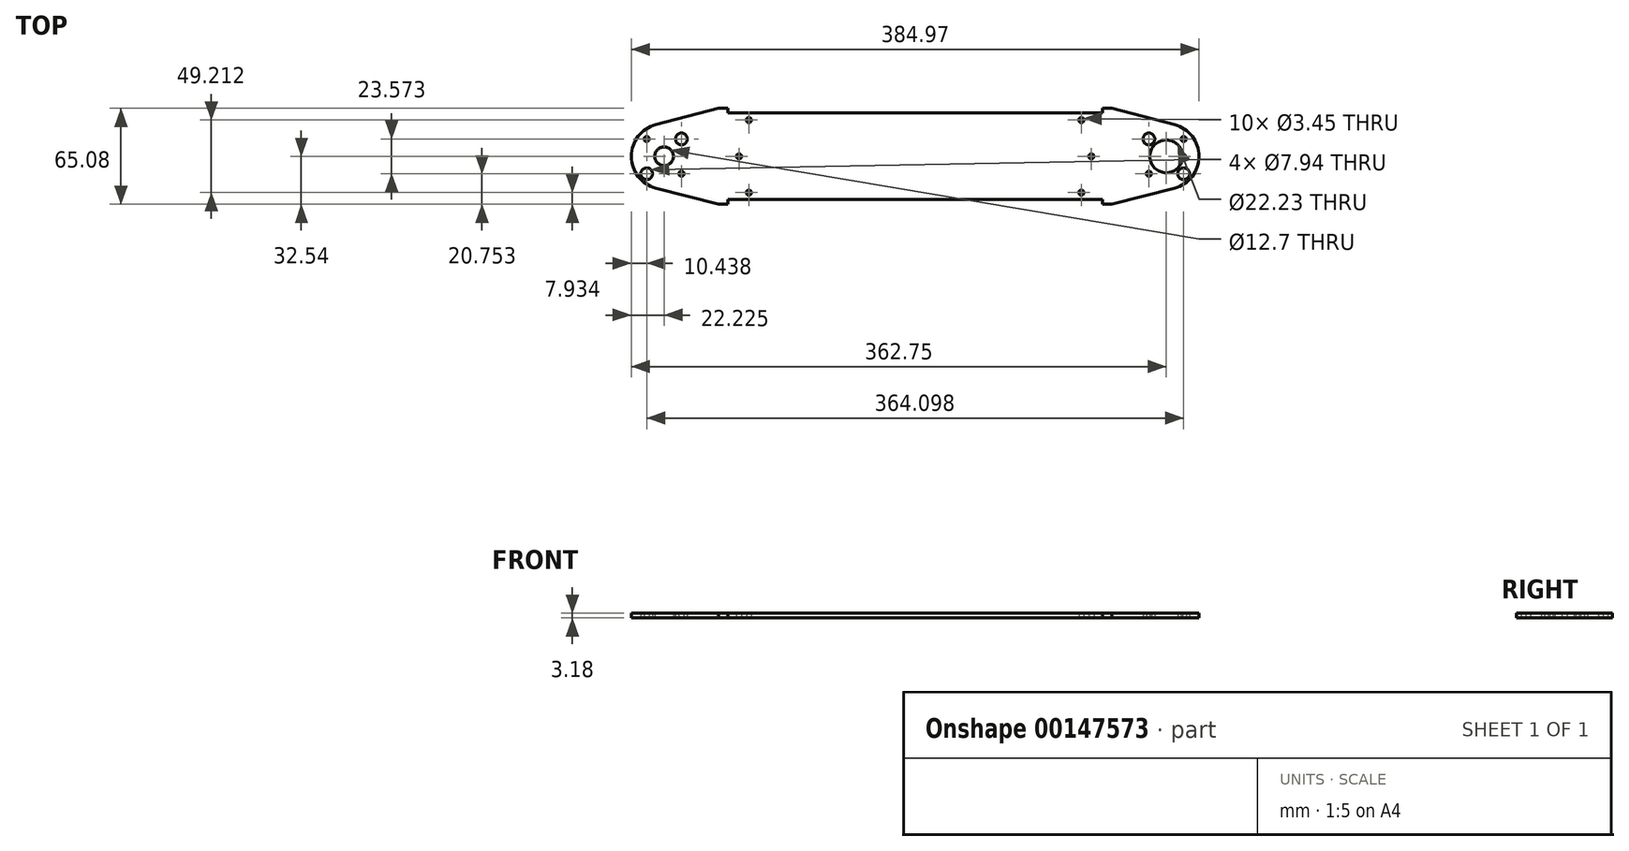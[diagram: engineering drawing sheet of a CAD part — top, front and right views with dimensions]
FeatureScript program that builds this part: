
annotation { "Feature Type Name" : "Feature", "Feature Type Description" : "" }
export const myFeature = defineFeature(function(context is Context, id is Id, definition is map)
    precondition{}
    {
        {
            var Q0;
            Q0=qCreatedBy(makeId("Top.planeOp"),FACE);
            var sketch = newSketch(context, id + "F0", { "sketchPlane" : qUnion([Q0])});
            skPoint(sketch, "E0.rect.middle", {"position": v(0, 0) * mm});
            skCircle(sketch, "E1", {"center": v(0, 0) * mm, "radius": 11.11 * mm});
            skLineSegment(sketch, "E2.bottom", {"start": v(11.79, 11.79) * mm, "end": v(-11.79, 11.79) * mm, "construction": true});
            skLineSegment(sketch, "E2.left", {"start": v(11.79, 11.79) * mm, "end": v(11.79, -11.79) * mm, "construction": true});
            skLineSegment(sketch, "E2.right", {"start": v(-11.79, 11.79) * mm, "end": v(-11.79, -11.79) * mm, "construction": true});
            skCircle(sketch, "E3", {"center": v(11.79, 11.79) * mm, "radius": 5.56 * mm, "construction": true});
            skCircle(sketch, "E4", {"center": v(-11.79, 11.79) * mm, "radius": 3.97 * mm});
            skCircle(sketch, "E5", {"center": v(11.79, 11.79) * mm, "radius": 1.73 * mm});
            skCircle(sketch, "E6", {"center": v(11.79, -11.79) * mm, "radius": 3.97 * mm});
            skCircle(sketch, "E7", {"center": v(-11.79, -11.79) * mm, "radius": 1.73 * mm});
            skArc(sketch, "E8", {"start": v(-346.1, 21.51) * mm, "mid": v(-362.75, 0) * mm, "end": v(-346.1, -21.51) * mm});
            skLineSegment(sketch, "E9.bottom", {"start": v(-352.31, 11.79) * mm, "end": v(-328.74, 11.79) * mm, "construction": true});
            skLineSegment(sketch, "E9.top", {"start": v(-352.31, -11.79) * mm, "end": v(-328.74, -11.79) * mm, "construction": true});
            skLineSegment(sketch, "E9.left", {"start": v(-352.31, 11.79) * mm, "end": v(-352.31, -11.79) * mm, "construction": true});
            skLineSegment(sketch, "E9.right", {"start": v(-328.74, 11.79) * mm, "end": v(-328.74, -11.79) * mm, "construction": true});
            skCircle(sketch, "E10", {"center": v(-328.74, 11.79) * mm, "radius": 3.97 * mm});
            skCircle(sketch, "E11", {"center": v(-352.31, 11.79) * mm, "radius": 1.73 * mm});
            skCircle(sketch, "E12", {"center": v(-352.31, -11.79) * mm, "radius": 3.97 * mm});
            skCircle(sketch, "E13", {"center": v(-328.74, -11.79) * mm, "radius": 1.73 * mm});
            skLineSegment(sketch, "E14", {"start": v(0, 0) * mm, "end": v(-340.53, 0) * mm, "construction": true});
            skLineSegment(sketch, "E15", {"start": v(-346.1, -21.51) * mm, "end": v(-303.61, -32.54) * mm});
            skLineSegment(sketch, "E16", {"start": v(-346.1, 21.51) * mm, "end": v(-303.61, 32.54) * mm});
            skLineSegment(sketch, "E17", {"start": v(-297.26, -29.37) * mm, "end": v(-43.26, -29.37) * mm});
            skLineSegment(sketch, "E18", {"start": v(-297.26, 29.37) * mm, "end": v(-43.26, 29.37) * mm});
            skLineSegment(sketch, "E19", {"start": v(-297.26, 32.54) * mm, "end": v(-297.26, 29.37) * mm});
            skLineSegment(sketch, "E20", {"start": v(-297.26, 32.54) * mm, "end": v(-303.61, 32.54) * mm});
            skLineSegment(sketch, "E21", {"start": v(-297.26, -29.37) * mm, "end": v(-297.26, -32.54) * mm});
            skLineSegment(sketch, "E22", {"start": v(-297.26, -32.54) * mm, "end": v(-303.61, -32.54) * mm});
            skLineSegment(sketch, "E23", {"start": v(-43.26, -29.37) * mm, "end": v(-43.26, -32.54) * mm});
            skLineSegment(sketch, "E24", {"start": v(-43.26, -32.54) * mm, "end": v(-36.91, -32.54) * mm});
            skLineSegment(sketch, "E25", {"start": v(-43.26, 29.37) * mm, "end": v(-43.26, 32.54) * mm});
            skLineSegment(sketch, "E26", {"start": v(-43.26, 32.54) * mm, "end": v(-36.91, 32.54) * mm});
            skLineSegment(sketch, "E27", {"start": v(-36.91, -32.54) * mm, "end": v(5.58, -21.51) * mm});
            skLineSegment(sketch, "E28", {"start": v(5.58, 21.51) * mm, "end": v(-36.91, 32.54) * mm});
            skArc(sketch, "E29", {"start": v(5.58, -21.51) * mm, "mid": v(22.23, 0) * mm, "end": v(5.58, 21.51) * mm});
            skLineSegment(sketch, "E30", {"start": v(-297.26, 29.37) * mm, "end": v(-297.26, 24.6) * mm, "construction": true});
            skLineSegment(sketch, "E31", {"start": v(-297.26, 24.6) * mm, "end": v(-282.98, 24.6) * mm, "construction": true});
            skLineSegment(sketch, "E32", {"start": v(-297.26, -29.37) * mm, "end": v(-297.26, -24.6) * mm, "construction": true});
            skLineSegment(sketch, "E33", {"start": v(-297.26, -24.6) * mm, "end": v(-282.98, -24.6) * mm, "construction": true});
            skLineSegment(sketch, "E34", {"start": v(-43.26, -29.37) * mm, "end": v(-43.26, -24.6) * mm, "construction": true});
            skLineSegment(sketch, "E35", {"start": v(-43.26, -24.6) * mm, "end": v(-57.55, -24.6) * mm, "construction": true});
            skLineSegment(sketch, "E36", {"start": v(-43.26, 29.37) * mm, "end": v(-43.26, 24.6) * mm, "construction": true});
            skLineSegment(sketch, "E37", {"start": v(-43.26, 24.6) * mm, "end": v(-57.55, 24.6) * mm, "construction": true});
            skCircle(sketch, "E38", {"center": v(-282.98, 24.6) * mm, "radius": 1.73 * mm});
            skCircle(sketch, "E39", {"center": v(-57.55, 24.6) * mm, "radius": 1.73 * mm});
            skCircle(sketch, "E40", {"center": v(-57.55, -24.6) * mm, "radius": 1.73 * mm});
            skCircle(sketch, "E41", {"center": v(-282.98, -24.6) * mm, "radius": 1.73 * mm});
            skLineSegment(sketch, "E42", {"start": v(-11.79, -11.79) * mm, "end": v(11.79, -11.79) * mm, "construction": true});
            skLineSegment(sketch, "E43", {"start": v(-170.26, -29.37) * mm, "end": v(-170.26, 0) * mm, "construction": true});
            skLineSegment(sketch, "E44", {"start": v(-170.26, 0) * mm, "end": v(-170.26, 29.37) * mm, "construction": true});
            skLineSegment(sketch, "E45", {"start": v(-328.74, 11.79) * mm, "end": v(-289.73, 11.79) * mm, "construction": true});
            skLineSegment(sketch, "E46", {"start": v(-289.73, 11.79) * mm, "end": v(-289.73, 0) * mm, "construction": true});
            skLineSegment(sketch, "E47", {"start": v(-11.79, 11.79) * mm, "end": v(-50.8, 11.79) * mm, "construction": true});
            skLineSegment(sketch, "E48", {"start": v(-50.8, 11.79) * mm, "end": v(-50.8, 0) * mm, "construction": true});
            skCircle(sketch, "E49", {"center": v(-50.8, 0) * mm, "radius": 1.73 * mm});
            skCircle(sketch, "E50", {"center": v(-289.73, 0) * mm, "radius": 1.73 * mm});
            skCircle(sketch, "E51", {"center": v(-340.53, 0) * mm, "radius": 6.35 * mm});
            skSolve(sketch);
        }
        {
            var Q0;
            Q0=qSketchRegion(id+"F0",true);
            extrude(context, id + "F1", {"entities" : qUnion([Q0]), "depth" : 3.17 * mm});
        }
    });
